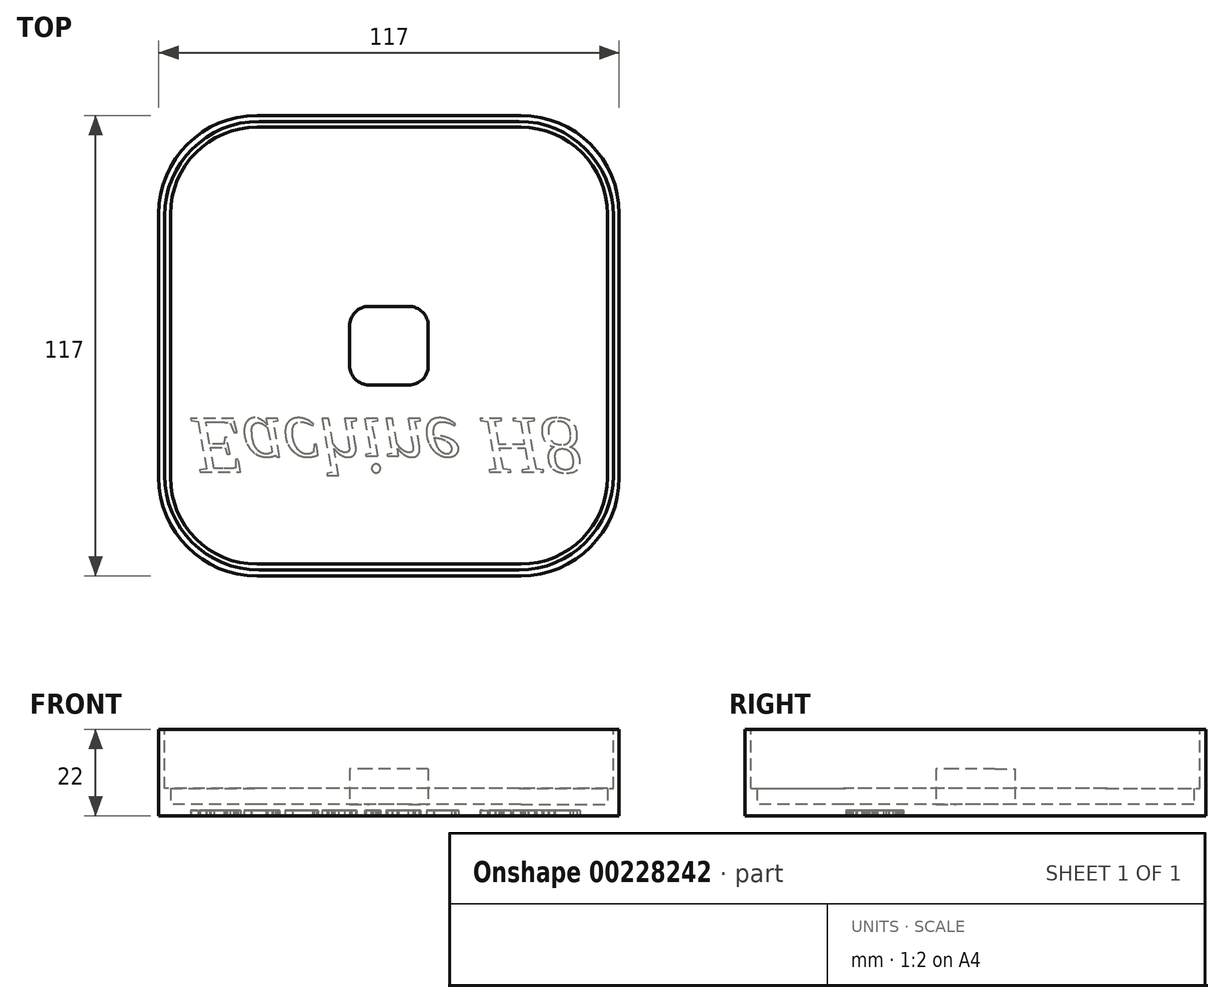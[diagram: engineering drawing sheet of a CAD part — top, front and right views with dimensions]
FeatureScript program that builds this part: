
annotation { "Feature Type Name" : "Feature", "Feature Type Description" : "" }
export const myFeature = defineFeature(function(context is Context, id is Id, definition is map)
    precondition{}
    {
        {
            var Q0;
            Q0=qCreatedBy(makeId("Top.planeOp"),FACE);
            var sketch = newSketch(context, id + "F0", { "sketchPlane" : qUnion([Q0])});
            skLineSegment(sketch, "E0.bottom", {"start": v(33.5, 58.5) * mm, "end": v(-33.5, 58.5) * mm});
            skLineSegment(sketch, "E0.top", {"start": v(33.5, -58.5) * mm, "end": v(-33.5, -58.5) * mm});
            skLineSegment(sketch, "E0.left", {"start": v(58.5, 33.5) * mm, "end": v(58.5, -33.5) * mm});
            skLineSegment(sketch, "E0.right", {"start": v(-58.5, 33.5) * mm, "end": v(-58.5, -33.5) * mm});
            skPoint(sketch, "E0.middle", {"position": v(0, 0) * mm});
            skPoint(sketch, "E1.visualSharp", {"position": v(-58.5, -58.5) * mm});
            skArc(sketch, "E1.filletArc", {"start": v(-58.5, -33.5) * mm, "mid": v(-51.18, -51.18) * mm, "end": v(-33.5, -58.5) * mm});
            skPoint(sketch, "E2.visualSharp", {"position": v(-58.5, 58.5) * mm});
            skArc(sketch, "E2.filletArc", {"start": v(-33.5, 58.5) * mm, "mid": v(-51.18, 51.18) * mm, "end": v(-58.5, 33.5) * mm});
            skPoint(sketch, "E3.visualSharp", {"position": v(58.5, 58.5) * mm});
            skArc(sketch, "E3.filletArc", {"start": v(58.5, 33.5) * mm, "mid": v(51.18, 51.18) * mm, "end": v(33.5, 58.5) * mm});
            skPoint(sketch, "E4.visualSharp", {"position": v(58.5, -58.5) * mm});
            skArc(sketch, "E4.filletArc", {"start": v(33.5, -58.5) * mm, "mid": v(51.18, -51.18) * mm, "end": v(58.5, -33.5) * mm});
            skSolve(sketch);
        }
        {
            var Q0;
            Q0 = qSketchRegion(id + "F0", true);
            extrude(context, id + "F1", {"entities" : qUnion([Q0]), "depth" : 22 * mm});
        }
        {
            var Q0;
            Q0=makeQuery(id+"F1.opExtrude","CAP_FACE",FACE,{"disambiguationData":[OSD([sQuery(id+"F0.wireOp",EDGE,"E0.bottom"),sQuery(id+"F0.wireOp",EDGE,"E0.top"),sQuery(id+"F0.wireOp",EDGE,"E0.left"),sQuery(id+"F0.wireOp",EDGE,"E0.right")])],"isStart":false});
            shell(context, id + "F2", {"entities" : qUnion([Q0]), "thickness" : 3 * mm});
        }
        {
            var Q0;
            Q0=makeQuery(id+"F1.opExtrude","CAP_FACE",FACE,{"disambiguationData":[OSD([sQuery(id+"F0.wireOp",EDGE,"E0.bottom"),sQuery(id+"F0.wireOp",EDGE,"E0.top"),sQuery(id+"F0.wireOp",EDGE,"E0.left"),sQuery(id+"F0.wireOp",EDGE,"E0.right")])],"isStart":false});
            var sketch = newSketch(context, id + "F3", { "sketchPlane" : qUnion([Q0])});
            skLineSegment(sketch, "E5.bottom", {"start": v(33, 57) * mm, "end": v(-33, 57) * mm});
            skLineSegment(sketch, "E5.top", {"start": v(33, -57) * mm, "end": v(-33, -57) * mm});
            skLineSegment(sketch, "E5.left", {"start": v(57, 33) * mm, "end": v(57, -33) * mm});
            skLineSegment(sketch, "E5.right", {"start": v(-57, 33) * mm, "end": v(-57, -33) * mm});
            skPoint(sketch, "E5.middle", {"position": v(0, 0) * mm});
            skLineSegment(sketch, "E6.bottom", {"start": v(33.5, 55.5) * mm, "end": v(-33.5, 55.5) * mm});
            skLineSegment(sketch, "E6.top", {"start": v(33.5, -55.5) * mm, "end": v(-33.5, -55.5) * mm});
            skLineSegment(sketch, "E6.left", {"start": v(33.5, 55.5) * mm, "end": v(33.5, -55.5) * mm});
            skLineSegment(sketch, "E6.right", {"start": v(-33.5, 55.5) * mm, "end": v(-33.5, -55.5) * mm});
            skPoint(sketch, "E7.visualSharp", {"position": v(-57, -57) * mm});
            skArc(sketch, "E7.filletArc", {"start": v(-57, -33) * mm, "mid": v(-49.97, -49.97) * mm, "end": v(-33, -57) * mm});
            skPoint(sketch, "E8.visualSharp", {"position": v(57, -57) * mm});
            skArc(sketch, "E8.filletArc", {"start": v(33, -57) * mm, "mid": v(49.97, -49.97) * mm, "end": v(57, -33) * mm});
            skPoint(sketch, "E9.visualSharp", {"position": v(57, 57) * mm});
            skArc(sketch, "E9.filletArc", {"start": v(57, 33) * mm, "mid": v(49.97, 49.97) * mm, "end": v(33, 57) * mm});
            skPoint(sketch, "E10.visualSharp", {"position": v(-57, 57) * mm});
            skArc(sketch, "E10.filletArc", {"start": v(-33, 57) * mm, "mid": v(-49.97, 49.97) * mm, "end": v(-57, 33) * mm});
            skSolve(sketch);
        }
        {
            var Q0;
            Q0 = qSketchRegion(id + "F3", true);
            extrude(context, id + "F4", {"entities" : qUnion([Q0]), "operationType" : NewBodyOperationType.REMOVE, "oppositeDirection" : true, "depth" : 15 * mm});
        }
        {
            var Q0;
            Q0=makeQuery(id+"F1.opExtrude","CAP_FACE",FACE,{"disambiguationData":[OSD([sQuery(id+"F0.wireOp",EDGE,"E0.bottom"),sQuery(id+"F0.wireOp",EDGE,"E0.top"),sQuery(id+"F0.wireOp",EDGE,"E0.left"),sQuery(id+"F0.wireOp",EDGE,"E0.right"),sQuery(id+"F0.wireOp",EDGE,"E1.filletArc"),sQuery(id+"F0.wireOp",EDGE,"E2.filletArc"),sQuery(id+"F0.wireOp",EDGE,"E3.filletArc"),sQuery(id+"F0.wireOp",EDGE,"E4.filletArc")])],"isStart":true});
            var sketch = newSketch(context, id + "F5", { "sketchPlane" : qUnion([Q0])});
            skText(sketch, "E11", { "text": "Eachine H8", "fontName": "Tinos-Italic.ttf"});
            const initialGuessF5  = {"E11": [-0.05012, 0.0185, 1, 0, 0.015]};
            skSetInitialGuess(sketch, initialGuessF5);
            skSolve(sketch);
        }
        {
            var Q0;
            Q0 = qSketchRegion(id + "F5", true);
            extrude(context, id + "F6", {"entities" : qUnion([Q0]), "operationType" : NewBodyOperationType.REMOVE, "oppositeDirection" : true, "depth" : 1.5 * mm});
        }
        {
            var Q0;
            Q0=makeQuery(id+"F2.opShell","OFFSET_FACE",FACE,{"disambiguationData":[OSD([sQuery(id+"F0.wireOp",EDGE,"E0.bottom"),sQuery(id+"F0.wireOp",EDGE,"E0.top"),sQuery(id+"F0.wireOp",EDGE,"E0.left"),sQuery(id+"F0.wireOp",EDGE,"E0.right"),sQuery(id+"F0.wireOp",EDGE,"E1.filletArc"),sQuery(id+"F0.wireOp",EDGE,"E2.filletArc"),sQuery(id+"F0.wireOp",EDGE,"E3.filletArc"),sQuery(id+"F0.wireOp",EDGE,"E4.filletArc")])]});
            var sketch = newSketch(context, id + "F7", { "sketchPlane" : qUnion([Q0])});
            skLineSegment(sketch, "E12.bottom", {"start": v(5, 10) * mm, "end": v(-5, 10) * mm});
            skLineSegment(sketch, "E12.top", {"start": v(5, -10) * mm, "end": v(-5, -10) * mm});
            skLineSegment(sketch, "E12.left", {"start": v(10, 5) * mm, "end": v(10, -5) * mm});
            skLineSegment(sketch, "E12.right", {"start": v(-10, 5) * mm, "end": v(-10, -5) * mm});
            skPoint(sketch, "E12.middle", {"position": v(0, 0) * mm});
            skPoint(sketch, "E13.visualSharp", {"position": v(-10, 10) * mm});
            skArc(sketch, "E13.filletArc", {"start": v(-5, 10) * mm, "mid": v(-8.54, 8.54) * mm, "end": v(-10, 5) * mm});
            skPoint(sketch, "E14.visualSharp", {"position": v(10, 10) * mm});
            skArc(sketch, "E14.filletArc", {"start": v(10, 5) * mm, "mid": v(8.54, 8.54) * mm, "end": v(5, 10) * mm});
            skPoint(sketch, "E15.visualSharp", {"position": v(10, -10) * mm});
            skArc(sketch, "E15.filletArc", {"start": v(5, -10) * mm, "mid": v(8.54, -8.54) * mm, "end": v(10, -5) * mm});
            skPoint(sketch, "E16.visualSharp", {"position": v(-10, -10) * mm});
            skArc(sketch, "E16.filletArc", {"start": v(-10, -5) * mm, "mid": v(-8.54, -8.54) * mm, "end": v(-5, -10) * mm});
            skSolve(sketch);
        }
        {
            var Q0;
            Q0 = qSketchRegion(id + "F7", true);
            extrude(context, id + "F8", {"entities" : qUnion([Q0]), "operationType" : NewBodyOperationType.ADD, "depth" : 9 * mm});
        }
    });
